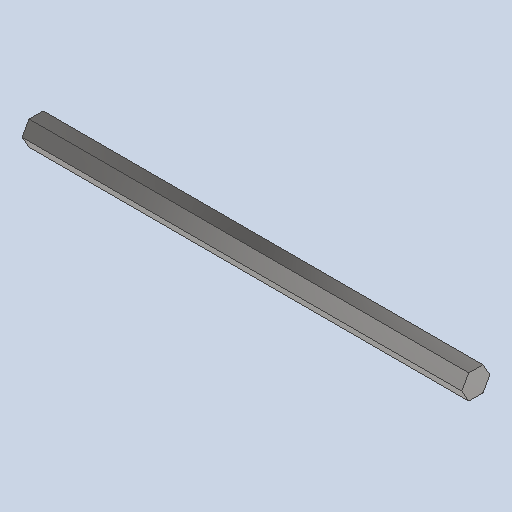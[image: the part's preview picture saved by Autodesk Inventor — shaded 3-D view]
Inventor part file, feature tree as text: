
AUTODESK INVENTOR PART (.ipt)
format: ipt  version: 2023 (Build 270158000, 158)  size: 88,576 bytes
history: native  units: in
note: dims shown in document units (in); Inventor stores cm internally (conversion verified against a paired STEP export)
features: other x3, sketch x1
ambient origin geometry x8: Origin, YZ Plane, XZ Plane, XY Plane, X Axis, Y Axis, Z Axis, Center Point
bodies: Solid1 (feature_tree)
feature tree (4):
  other  "9in-0.5inHexAxel_MIR1.ipt"
  other  "Solid1::9in-0.5inHexAxel_MIR1.ipt"
  other  "TaggingFeature1"
  sketch  "Sketch1"  dims[d0=0.3937in]
